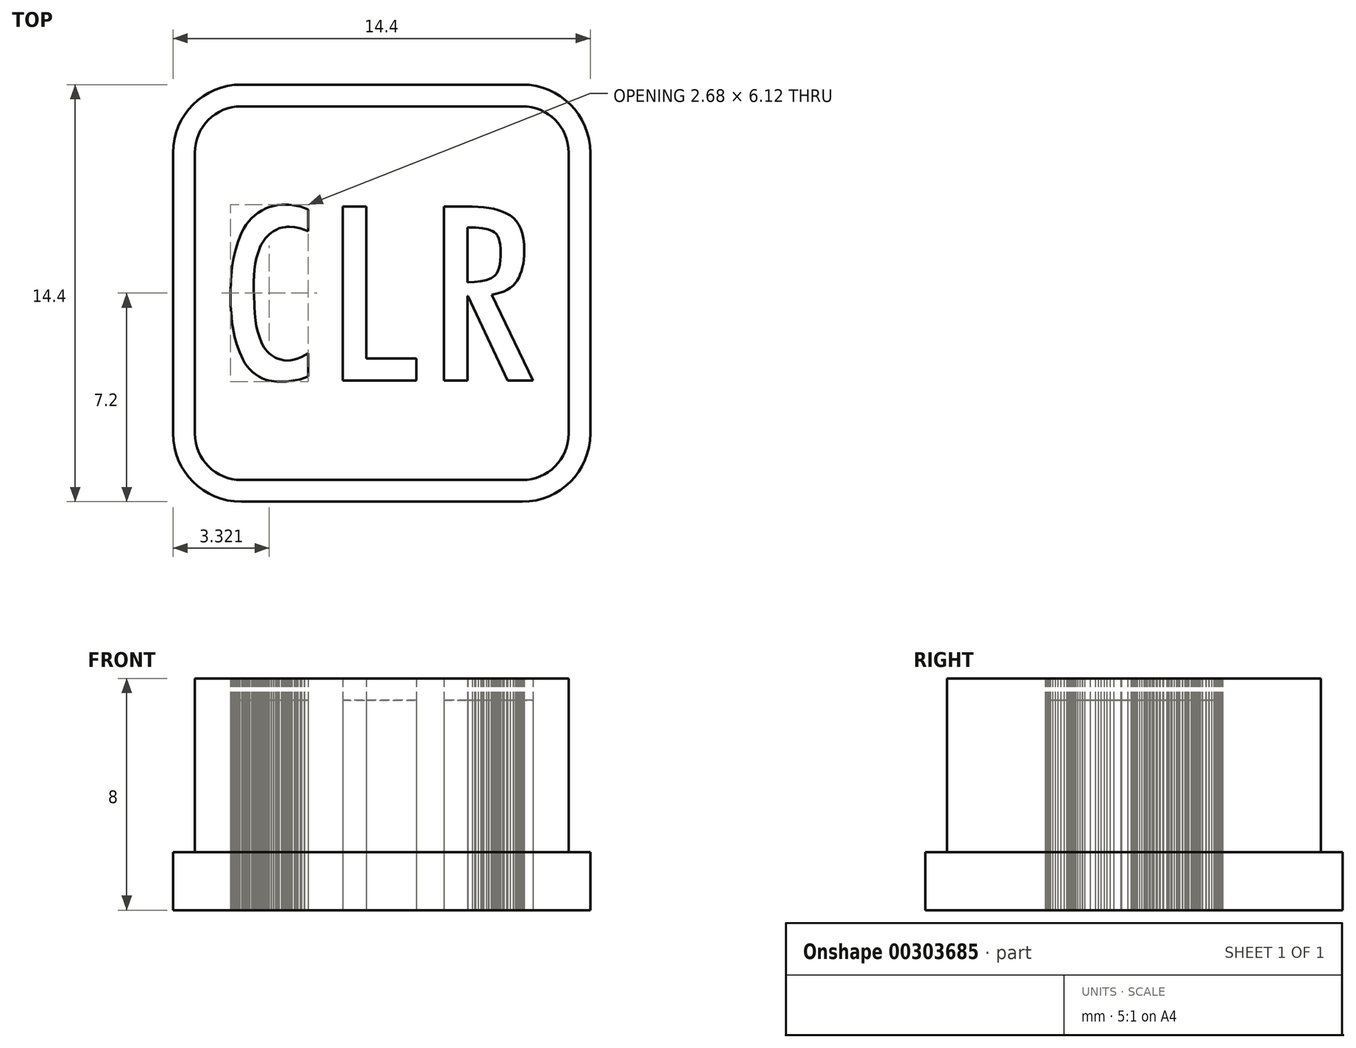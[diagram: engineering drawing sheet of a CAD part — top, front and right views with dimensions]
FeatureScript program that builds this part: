
annotation { "Feature Type Name" : "Feature", "Feature Type Description" : "" }
export const myFeature = defineFeature(function(context is Context, id is Id, definition is map)
    precondition{}
    {
        {
            var Q0;
            Q0=qCreatedBy(makeId("Top.planeOp"),FACE);
            var sketch = newSketch(context, id + "F0", { "sketchPlane" : qUnion([Q0])});
            skArc(sketch, "E0", {"start": v(4.85, -6.45) * mm, "mid": v(5.98, -5.98) * mm, "end": v(6.45, -4.85) * mm});
            skLineSegment(sketch, "E1", {"start": v(6.45, -4.85) * mm, "end": v(6.45, 4.85) * mm});
            skArc(sketch, "E2", {"start": v(6.45, 4.85) * mm, "mid": v(5.98, 5.98) * mm, "end": v(4.85, 6.45) * mm});
            skLineSegment(sketch, "E3", {"start": v(4.85, 6.45) * mm, "end": v(-4.85, 6.45) * mm});
            skArc(sketch, "E4", {"start": v(-4.85, 6.45) * mm, "mid": v(-5.98, 5.98) * mm, "end": v(-6.45, 4.85) * mm});
            skLineSegment(sketch, "E5", {"start": v(-6.45, 4.85) * mm, "end": v(-6.45, -4.85) * mm});
            skArc(sketch, "E6", {"start": v(-6.45, -4.85) * mm, "mid": v(-5.98, -5.98) * mm, "end": v(-4.85, -6.45) * mm});
            skLineSegment(sketch, "E7", {"start": v(-4.85, -6.45) * mm, "end": v(4.85, -6.45) * mm});
            skArc(sketch, "E8", {"start": v(-4.85, 7.2) * mm, "mid": v(-6.51, 6.51) * mm, "end": v(-7.2, 4.85) * mm});
            skLineSegment(sketch, "E9", {"start": v(-7.2, 4.85) * mm, "end": v(-7.2, -4.85) * mm});
            skArc(sketch, "E10", {"start": v(-7.2, -4.85) * mm, "mid": v(-6.51, -6.51) * mm, "end": v(-4.85, -7.2) * mm});
            skLineSegment(sketch, "E11", {"start": v(-4.85, -7.2) * mm, "end": v(4.85, -7.2) * mm});
            skArc(sketch, "E12", {"start": v(4.85, -7.2) * mm, "mid": v(6.51, -6.51) * mm, "end": v(7.2, -4.85) * mm});
            skLineSegment(sketch, "E13", {"start": v(7.2, -4.85) * mm, "end": v(7.2, 4.85) * mm});
            skArc(sketch, "E14", {"start": v(7.2, 4.85) * mm, "mid": v(6.51, 6.51) * mm, "end": v(4.85, 7.2) * mm});
            skLineSegment(sketch, "E15", {"start": v(4.85, 7.2) * mm, "end": v(-4.85, 7.2) * mm});
            skLineSegment(sketch, "E16", {"start": v(-2.54, -2.88) * mm, "end": v(-2.67, -2.93) * mm});
            skLineSegment(sketch, "E17", {"start": v(-2.67, -2.93) * mm, "end": v(-2.82, -2.97) * mm});
            skLineSegment(sketch, "E18", {"start": v(-2.82, -2.97) * mm, "end": v(-2.98, -3) * mm});
            skLineSegment(sketch, "E19", {"start": v(-2.98, -3) * mm, "end": v(-3.13, -3.03) * mm});
            skLineSegment(sketch, "E20", {"start": v(-3.13, -3.03) * mm, "end": v(-3.3, -3.05) * mm});
            skLineSegment(sketch, "E21", {"start": v(-3.3, -3.05) * mm, "end": v(-3.44, -3.06) * mm});
            skLineSegment(sketch, "E22", {"start": v(-3.44, -3.06) * mm, "end": v(-3.62, -3.05) * mm});
            skLineSegment(sketch, "E23", {"start": v(-3.62, -3.05) * mm, "end": v(-3.81, -3.03) * mm});
            skLineSegment(sketch, "E24", {"start": v(-3.81, -3.03) * mm, "end": v(-3.9, -3.02) * mm});
            skLineSegment(sketch, "E25", {"start": v(-3.9, -3.02) * mm, "end": v(-4, -3) * mm});
            skLineSegment(sketch, "E26", {"start": v(-4, -3) * mm, "end": v(-4.12, -2.94) * mm});
            skLineSegment(sketch, "E27", {"start": v(-4.12, -2.94) * mm, "end": v(-4.25, -2.88) * mm});
            skLineSegment(sketch, "E28", {"start": v(-4.25, -2.88) * mm, "end": v(-4.36, -2.8) * mm});
            skLineSegment(sketch, "E29", {"start": v(-4.36, -2.8) * mm, "end": v(-4.46, -2.72) * mm});
            skLineSegment(sketch, "E30", {"start": v(-4.46, -2.72) * mm, "end": v(-4.56, -2.63) * mm});
            skLineSegment(sketch, "E31", {"start": v(-4.56, -2.63) * mm, "end": v(-4.64, -2.53) * mm});
            skLineSegment(sketch, "E32", {"start": v(-4.64, -2.53) * mm, "end": v(-4.72, -2.41) * mm});
            skLineSegment(sketch, "E33", {"start": v(-4.72, -2.41) * mm, "end": v(-4.79, -2.3) * mm});
            skLineSegment(sketch, "E34", {"start": v(-4.79, -2.3) * mm, "end": v(-4.9, -2.04) * mm});
            skLineSegment(sketch, "E35", {"start": v(-4.9, -2.04) * mm, "end": v(-5, -1.78) * mm});
            skLineSegment(sketch, "E36", {"start": v(-5, -1.78) * mm, "end": v(-5.07, -1.5) * mm});
            skLineSegment(sketch, "E37", {"start": v(-5.07, -1.5) * mm, "end": v(-5.13, -1.23) * mm});
            skLineSegment(sketch, "E38", {"start": v(-5.13, -1.23) * mm, "end": v(-5.16, -1.03) * mm});
            skLineSegment(sketch, "E39", {"start": v(-5.16, -1.03) * mm, "end": v(-5.18, -0.82) * mm});
            skLineSegment(sketch, "E40", {"start": v(-5.18, -0.82) * mm, "end": v(-5.21, -0.43) * mm});
            skLineSegment(sketch, "E41", {"start": v(-5.21, -0.43) * mm, "end": v(-5.21, -0.32) * mm});
            skLineSegment(sketch, "E42", {"start": v(-5.21, -0.32) * mm, "end": v(-5.21, -0.21) * mm});
            skLineSegment(sketch, "E43", {"start": v(-5.21, -0.21) * mm, "end": v(-5.22, -0.1) * mm});
            skLineSegment(sketch, "E44", {"start": v(-5.22, -0.1) * mm, "end": v(-5.22, 0.02) * mm});
            skLineSegment(sketch, "E45", {"start": v(-5.22, 0.02) * mm, "end": v(-5.2, 0.45) * mm});
            skLineSegment(sketch, "E46", {"start": v(-5.2, 0.45) * mm, "end": v(-5.17, 0.9) * mm});
            skLineSegment(sketch, "E47", {"start": v(-5.17, 0.9) * mm, "end": v(-5.12, 1.2) * mm});
            skLineSegment(sketch, "E48", {"start": v(-5.12, 1.2) * mm, "end": v(-5.05, 1.5) * mm});
            skLineSegment(sketch, "E49", {"start": v(-5.05, 1.5) * mm, "end": v(-4.95, 1.8) * mm});
            skLineSegment(sketch, "E50", {"start": v(-4.95, 1.8) * mm, "end": v(-4.83, 2.09) * mm});
            skLineSegment(sketch, "E51", {"start": v(-4.83, 2.09) * mm, "end": v(-4.76, 2.23) * mm});
            skLineSegment(sketch, "E52", {"start": v(-4.76, 2.23) * mm, "end": v(-4.68, 2.35) * mm});
            skLineSegment(sketch, "E53", {"start": v(-4.68, 2.35) * mm, "end": v(-4.6, 2.47) * mm});
            skLineSegment(sketch, "E54", {"start": v(-4.6, 2.47) * mm, "end": v(-4.5, 2.58) * mm});
            skLineSegment(sketch, "E55", {"start": v(-4.5, 2.58) * mm, "end": v(-4.39, 2.68) * mm});
            skLineSegment(sketch, "E56", {"start": v(-4.39, 2.68) * mm, "end": v(-4.27, 2.77) * mm});
            skLineSegment(sketch, "E57", {"start": v(-4.27, 2.77) * mm, "end": v(-4.14, 2.85) * mm});
            skLineSegment(sketch, "E58", {"start": v(-4.14, 2.85) * mm, "end": v(-4, 2.92) * mm});
            skLineSegment(sketch, "E59", {"start": v(-4, 2.92) * mm, "end": v(-3.9, 2.96) * mm});
            skLineSegment(sketch, "E60", {"start": v(-3.9, 2.96) * mm, "end": v(-3.81, 3) * mm});
            skLineSegment(sketch, "E61", {"start": v(-3.81, 3) * mm, "end": v(-3.6, 3.04) * mm});
            skLineSegment(sketch, "E62", {"start": v(-3.6, 3.04) * mm, "end": v(-3.46, 3.05) * mm});
            skLineSegment(sketch, "E63", {"start": v(-3.46, 3.05) * mm, "end": v(-3.33, 3.06) * mm});
            skLineSegment(sketch, "E64", {"start": v(-3.33, 3.06) * mm, "end": v(-3.21, 3.05) * mm});
            skLineSegment(sketch, "E65", {"start": v(-3.21, 3.05) * mm, "end": v(-3.1, 3.04) * mm});
            skLineSegment(sketch, "E66", {"start": v(-3.1, 3.04) * mm, "end": v(-2.95, 3.02) * mm});
            skLineSegment(sketch, "E67", {"start": v(-2.95, 3.02) * mm, "end": v(-2.8, 2.99) * mm});
            skLineSegment(sketch, "E68", {"start": v(-2.8, 2.99) * mm, "end": v(-2.67, 2.95) * mm});
            skLineSegment(sketch, "E69", {"start": v(-2.67, 2.95) * mm, "end": v(-2.54, 2.9) * mm});
            skLineSegment(sketch, "E70", {"start": v(-2.54, 2.9) * mm, "end": v(-2.54, 2.13) * mm});
            skLineSegment(sketch, "E71", {"start": v(-2.54, 2.13) * mm, "end": v(-2.67, 2.19) * mm});
            skLineSegment(sketch, "E72", {"start": v(-2.67, 2.19) * mm, "end": v(-2.82, 2.24) * mm});
            skLineSegment(sketch, "E73", {"start": v(-2.82, 2.24) * mm, "end": v(-3, 2.28) * mm});
            skLineSegment(sketch, "E74", {"start": v(-3, 2.28) * mm, "end": v(-3.19, 2.3) * mm});
            skLineSegment(sketch, "E75", {"start": v(-3.19, 2.3) * mm, "end": v(-3.26, 2.3) * mm});
            skLineSegment(sketch, "E76", {"start": v(-3.26, 2.3) * mm, "end": v(-3.33, 2.28) * mm});
            skLineSegment(sketch, "E77", {"start": v(-3.33, 2.28) * mm, "end": v(-3.43, 2.26) * mm});
            skLineSegment(sketch, "E78", {"start": v(-3.43, 2.26) * mm, "end": v(-3.54, 2.24) * mm});
            skLineSegment(sketch, "E79", {"start": v(-3.54, 2.24) * mm, "end": v(-3.63, 2.2) * mm});
            skLineSegment(sketch, "E80", {"start": v(-3.63, 2.2) * mm, "end": v(-3.73, 2.13) * mm});
            skLineSegment(sketch, "E81", {"start": v(-3.73, 2.13) * mm, "end": v(-3.8, 2.08) * mm});
            skLineSegment(sketch, "E82", {"start": v(-3.8, 2.08) * mm, "end": v(-3.88, 2.03) * mm});
            skLineSegment(sketch, "E83", {"start": v(-3.88, 2.03) * mm, "end": v(-3.95, 1.97) * mm});
            skLineSegment(sketch, "E84", {"start": v(-3.95, 1.97) * mm, "end": v(-4.01, 1.9) * mm});
            skLineSegment(sketch, "E85", {"start": v(-4.01, 1.9) * mm, "end": v(-4.07, 1.83) * mm});
            skLineSegment(sketch, "E86", {"start": v(-4.07, 1.83) * mm, "end": v(-4.12, 1.75) * mm});
            skLineSegment(sketch, "E87", {"start": v(-4.12, 1.75) * mm, "end": v(-4.17, 1.66) * mm});
            skLineSegment(sketch, "E88", {"start": v(-4.17, 1.66) * mm, "end": v(-4.2, 1.58) * mm});
            skLineSegment(sketch, "E89", {"start": v(-4.2, 1.58) * mm, "end": v(-4.27, 1.4) * mm});
            skLineSegment(sketch, "E90", {"start": v(-4.27, 1.4) * mm, "end": v(-4.33, 1.2) * mm});
            skLineSegment(sketch, "E91", {"start": v(-4.33, 1.2) * mm, "end": v(-4.37, 1) * mm});
            skLineSegment(sketch, "E92", {"start": v(-4.37, 1) * mm, "end": v(-4.4, 0.8) * mm});
            skLineSegment(sketch, "E93", {"start": v(-4.4, 0.8) * mm, "end": v(-4.42, 0.42) * mm});
            skLineSegment(sketch, "E94", {"start": v(-4.42, 0.42) * mm, "end": v(-4.42, 0.05) * mm});
            skLineSegment(sketch, "E95", {"start": v(-4.42, 0.05) * mm, "end": v(-4.42, 0.03) * mm});
            skLineSegment(sketch, "E96", {"start": v(-4.42, 0.03) * mm, "end": v(-4.42, 0.03) * mm});
            skLineSegment(sketch, "E97", {"start": v(-4.42, 0.03) * mm, "end": v(-4.42, 0.01) * mm});
            skLineSegment(sketch, "E98", {"start": v(-4.42, 0.01) * mm, "end": v(-4.42, 0) * mm});
            skLineSegment(sketch, "E99", {"start": v(-4.42, 0) * mm, "end": v(-4.41, -0.02) * mm});
            skLineSegment(sketch, "E100", {"start": v(-4.41, -0.02) * mm, "end": v(-4.4, -0.03) * mm});
            skLineSegment(sketch, "E101", {"start": v(-4.4, -0.03) * mm, "end": v(-4.4, -0.46) * mm});
            skLineSegment(sketch, "E102", {"start": v(-4.4, -0.46) * mm, "end": v(-4.38, -0.7) * mm});
            skLineSegment(sketch, "E103", {"start": v(-4.38, -0.7) * mm, "end": v(-4.36, -0.94) * mm});
            skLineSegment(sketch, "E104", {"start": v(-4.36, -0.94) * mm, "end": v(-4.33, -1.14) * mm});
            skLineSegment(sketch, "E105", {"start": v(-4.33, -1.14) * mm, "end": v(-4.28, -1.33) * mm});
            skLineSegment(sketch, "E106", {"start": v(-4.28, -1.33) * mm, "end": v(-4.22, -1.52) * mm});
            skLineSegment(sketch, "E107", {"start": v(-4.22, -1.52) * mm, "end": v(-4.15, -1.7) * mm});
            skLineSegment(sketch, "E108", {"start": v(-4.15, -1.7) * mm, "end": v(-4.1, -1.79) * mm});
            skLineSegment(sketch, "E109", {"start": v(-4.1, -1.79) * mm, "end": v(-4.06, -1.87) * mm});
            skLineSegment(sketch, "E110", {"start": v(-4.06, -1.87) * mm, "end": v(-4, -1.94) * mm});
            skLineSegment(sketch, "E111", {"start": v(-4, -1.94) * mm, "end": v(-3.95, -2.01) * mm});
            skLineSegment(sketch, "E112", {"start": v(-3.95, -2.01) * mm, "end": v(-3.89, -2.07) * mm});
            skLineSegment(sketch, "E113", {"start": v(-3.89, -2.07) * mm, "end": v(-3.82, -2.13) * mm});
            skLineSegment(sketch, "E114", {"start": v(-3.82, -2.13) * mm, "end": v(-3.74, -2.18) * mm});
            skLineSegment(sketch, "E115", {"start": v(-3.74, -2.18) * mm, "end": v(-3.66, -2.23) * mm});
            skLineSegment(sketch, "E116", {"start": v(-3.66, -2.23) * mm, "end": v(-3.57, -2.27) * mm});
            skLineSegment(sketch, "E117", {"start": v(-3.57, -2.27) * mm, "end": v(-3.47, -2.3) * mm});
            skLineSegment(sketch, "E118", {"start": v(-3.47, -2.3) * mm, "end": v(-3.38, -2.32) * mm});
            skLineSegment(sketch, "E119", {"start": v(-3.38, -2.32) * mm, "end": v(-3.28, -2.33) * mm});
            skLineSegment(sketch, "E120", {"start": v(-3.28, -2.33) * mm, "end": v(-3.15, -2.32) * mm});
            skLineSegment(sketch, "E121", {"start": v(-3.15, -2.32) * mm, "end": v(-3.02, -2.3) * mm});
            skLineSegment(sketch, "E122", {"start": v(-3.02, -2.3) * mm, "end": v(-2.9, -2.25) * mm});
            skLineSegment(sketch, "E123", {"start": v(-2.9, -2.25) * mm, "end": v(-2.77, -2.2) * mm});
            skLineSegment(sketch, "E124", {"start": v(-2.77, -2.2) * mm, "end": v(-2.54, -2.08) * mm});
            skLineSegment(sketch, "E125", {"start": v(-2.54, -2.08) * mm, "end": v(-2.54, -2.88) * mm});
            skLineSegment(sketch, "E126", {"start": v(-1.35, -3.01) * mm, "end": v(-1.35, 2.99) * mm});
            skLineSegment(sketch, "E127", {"start": v(-1.35, 2.99) * mm, "end": v(-0.53, 2.99) * mm});
            skLineSegment(sketch, "E128", {"start": v(-0.53, 2.99) * mm, "end": v(-0.53, -2.25) * mm});
            skLineSegment(sketch, "E129", {"start": v(-0.53, -2.25) * mm, "end": v(1.2, -2.25) * mm});
            skLineSegment(sketch, "E130", {"start": v(1.2, -2.25) * mm, "end": v(1.2, -3.01) * mm});
            skLineSegment(sketch, "E131", {"start": v(1.2, -3.01) * mm, "end": v(-1.35, -3.01) * mm});
            skLineSegment(sketch, "E132", {"start": v(2.96, -0.1) * mm, "end": v(2.96, -3.01) * mm});
            skLineSegment(sketch, "E133", {"start": v(2.96, -3.01) * mm, "end": v(2.14, -3.01) * mm});
            skLineSegment(sketch, "E134", {"start": v(2.14, -3.01) * mm, "end": v(2.14, 2.99) * mm});
            skLineSegment(sketch, "E135", {"start": v(2.14, 2.99) * mm, "end": v(3.12, 2.99) * mm});
            skLineSegment(sketch, "E136", {"start": v(3.12, 2.99) * mm, "end": v(3.32, 2.98) * mm});
            skLineSegment(sketch, "E137", {"start": v(3.32, 2.98) * mm, "end": v(3.51, 2.97) * mm});
            skLineSegment(sketch, "E138", {"start": v(3.51, 2.97) * mm, "end": v(3.7, 2.94) * mm});
            skLineSegment(sketch, "E139", {"start": v(3.7, 2.94) * mm, "end": v(3.86, 2.9) * mm});
            skLineSegment(sketch, "E140", {"start": v(3.86, 2.9) * mm, "end": v(4.02, 2.87) * mm});
            skLineSegment(sketch, "E141", {"start": v(4.02, 2.87) * mm, "end": v(4.17, 2.81) * mm});
            skLineSegment(sketch, "E142", {"start": v(4.17, 2.81) * mm, "end": v(4.3, 2.75) * mm});
            skLineSegment(sketch, "E143", {"start": v(4.3, 2.75) * mm, "end": v(4.43, 2.68) * mm});
            skLineSegment(sketch, "E144", {"start": v(4.43, 2.68) * mm, "end": v(4.55, 2.6) * mm});
            skLineSegment(sketch, "E145", {"start": v(4.55, 2.6) * mm, "end": v(4.65, 2.49) * mm});
            skLineSegment(sketch, "E146", {"start": v(4.65, 2.49) * mm, "end": v(4.73, 2.36) * mm});
            skLineSegment(sketch, "E147", {"start": v(4.73, 2.36) * mm, "end": v(4.8, 2.22) * mm});
            skLineSegment(sketch, "E148", {"start": v(4.8, 2.22) * mm, "end": v(4.85, 2.06) * mm});
            skLineSegment(sketch, "E149", {"start": v(4.85, 2.06) * mm, "end": v(4.89, 1.88) * mm});
            skLineSegment(sketch, "E150", {"start": v(4.89, 1.88) * mm, "end": v(4.91, 1.68) * mm});
            skLineSegment(sketch, "E151", {"start": v(4.91, 1.68) * mm, "end": v(4.92, 1.46) * mm});
            skLineSegment(sketch, "E152", {"start": v(4.92, 1.46) * mm, "end": v(4.92, 1.3) * mm});
            skLineSegment(sketch, "E153", {"start": v(4.92, 1.3) * mm, "end": v(4.9, 1.16) * mm});
            skLineSegment(sketch, "E154", {"start": v(4.9, 1.16) * mm, "end": v(4.88, 1.02) * mm});
            skLineSegment(sketch, "E155", {"start": v(4.88, 1.02) * mm, "end": v(4.86, 0.9) * mm});
            skLineSegment(sketch, "E156", {"start": v(4.86, 0.9) * mm, "end": v(4.82, 0.77) * mm});
            skLineSegment(sketch, "E157", {"start": v(4.82, 0.77) * mm, "end": v(4.78, 0.65) * mm});
            skLineSegment(sketch, "E158", {"start": v(4.78, 0.65) * mm, "end": v(4.73, 0.54) * mm});
            skLineSegment(sketch, "E159", {"start": v(4.73, 0.54) * mm, "end": v(4.68, 0.44) * mm});
            skLineSegment(sketch, "E160", {"start": v(4.68, 0.44) * mm, "end": v(4.6, 0.35) * mm});
            skLineSegment(sketch, "E161", {"start": v(4.6, 0.35) * mm, "end": v(4.53, 0.26) * mm});
            skLineSegment(sketch, "E162", {"start": v(4.53, 0.26) * mm, "end": v(4.44, 0.19) * mm});
            skLineSegment(sketch, "E163", {"start": v(4.44, 0.19) * mm, "end": v(4.33, 0.12) * mm});
            skLineSegment(sketch, "E164", {"start": v(4.33, 0.12) * mm, "end": v(4.22, 0.06) * mm});
            skLineSegment(sketch, "E165", {"start": v(4.22, 0.06) * mm, "end": v(4.09, 0.01) * mm});
            skLineSegment(sketch, "E166", {"start": v(4.09, 0.01) * mm, "end": v(3.95, -0.03) * mm});
            skLineSegment(sketch, "E167", {"start": v(3.95, -0.03) * mm, "end": v(3.8, -0.05) * mm});
            skLineSegment(sketch, "E168", {"start": v(3.8, -0.05) * mm, "end": v(5.22, -3.01) * mm});
            skLineSegment(sketch, "E169", {"start": v(5.22, -3.01) * mm, "end": v(4.34, -3.01) * mm});
            skLineSegment(sketch, "E170", {"start": v(4.34, -3.01) * mm, "end": v(2.98, -0.1) * mm});
            skLineSegment(sketch, "E171", {"start": v(2.98, -0.1) * mm, "end": v(2.96, -0.1) * mm});
            skLineSegment(sketch, "E172", {"start": v(2.96, 2.27) * mm, "end": v(2.96, 0.38) * mm});
            skLineSegment(sketch, "E173", {"start": v(2.96, 0.38) * mm, "end": v(3.2, 0.38) * mm});
            skLineSegment(sketch, "E174", {"start": v(3.2, 0.38) * mm, "end": v(3.42, 0.41) * mm});
            skLineSegment(sketch, "E175", {"start": v(3.42, 0.41) * mm, "end": v(3.6, 0.46) * mm});
            skLineSegment(sketch, "E176", {"start": v(3.6, 0.46) * mm, "end": v(3.78, 0.52) * mm});
            skLineSegment(sketch, "E177", {"start": v(3.78, 0.52) * mm, "end": v(3.85, 0.56) * mm});
            skLineSegment(sketch, "E178", {"start": v(3.85, 0.56) * mm, "end": v(3.92, 0.62) * mm});
            skLineSegment(sketch, "E179", {"start": v(3.92, 0.62) * mm, "end": v(3.97, 0.7) * mm});
            skLineSegment(sketch, "E180", {"start": v(3.97, 0.7) * mm, "end": v(4.02, 0.78) * mm});
            skLineSegment(sketch, "E181", {"start": v(4.02, 0.78) * mm, "end": v(4.05, 0.88) * mm});
            skLineSegment(sketch, "E182", {"start": v(4.05, 0.88) * mm, "end": v(4.08, 1) * mm});
            skLineSegment(sketch, "E183", {"start": v(4.08, 1) * mm, "end": v(4.1, 1.13) * mm});
            skLineSegment(sketch, "E184", {"start": v(4.1, 1.13) * mm, "end": v(4.1, 1.27) * mm});
            skLineSegment(sketch, "E185", {"start": v(4.1, 1.27) * mm, "end": v(4.1, 1.38) * mm});
            skLineSegment(sketch, "E186", {"start": v(4.1, 1.38) * mm, "end": v(4.1, 1.53) * mm});
            skLineSegment(sketch, "E187", {"start": v(4.1, 1.53) * mm, "end": v(4.09, 1.67) * mm});
            skLineSegment(sketch, "E188", {"start": v(4.09, 1.67) * mm, "end": v(4.07, 1.79) * mm});
            skLineSegment(sketch, "E189", {"start": v(4.07, 1.79) * mm, "end": v(4.04, 1.89) * mm});
            skLineSegment(sketch, "E190", {"start": v(4.04, 1.89) * mm, "end": v(4, 1.98) * mm});
            skLineSegment(sketch, "E191", {"start": v(4, 1.98) * mm, "end": v(3.95, 2.05) * mm});
            skLineSegment(sketch, "E192", {"start": v(3.95, 2.05) * mm, "end": v(3.9, 2.1) * mm});
            skLineSegment(sketch, "E193", {"start": v(3.9, 2.1) * mm, "end": v(3.83, 2.14) * mm});
            skLineSegment(sketch, "E194", {"start": v(3.83, 2.14) * mm, "end": v(3.67, 2.2) * mm});
            skLineSegment(sketch, "E195", {"start": v(3.67, 2.2) * mm, "end": v(3.47, 2.24) * mm});
            skLineSegment(sketch, "E196", {"start": v(3.47, 2.24) * mm, "end": v(3.24, 2.26) * mm});
            skLineSegment(sketch, "E197", {"start": v(3.24, 2.26) * mm, "end": v(2.96, 2.27) * mm});
            skSolve(sketch);
        }
        {
            var Q0;
            Q0=makeQuery(id+"F0.imprint","IMPRINT",FACE,{"disambiguationData":[TD([[makeQuery(id+"F0.imprint","IMPRINT",EDGE,{"derivedFrom":sQuery(id+"F0.wireOp",EDGE,"E0")}),-1.0]])]});
            extrude(context, id + "F1", {"entities" : qUnion([Q0]), "depth" : 2 * mm});
        }
        {
            var Q0;
            Q0=makeQuery(id+"F0.imprint","IMPRINT",FACE,{"disambiguationData":[TD([[makeQuery(id+"F0.imprint","IMPRINT",EDGE,{"derivedFrom":sQuery(id+"F0.wireOp",EDGE,"E0")}),1.0]])]});
            var Q1;
            Q1=makeQuery(id+"F0.imprint","IMPRINT",FACE,{"disambiguationData":[TD([[makeQuery(id+"F0.imprint","IMPRINT",EDGE,{"derivedFrom":sQuery(id+"F0.wireOp",EDGE,"E172")}),1.0]])]});
            extrude(context, id + "F2", {"entities" : qUnion([Q0, Q1]), "operationType" : NewBodyOperationType.ADD, "depth" : 8 * mm});
        }
        {
            var Q0;
            Q0=makeQuery(id+"F0.imprint","IMPRINT",FACE,{"disambiguationData":[TD([[makeQuery(id+"F0.imprint","IMPRINT",EDGE,{"derivedFrom":sQuery(id+"F0.wireOp",EDGE,"E16")}),-1.0]])]});
            var Q1;
            Q1=makeQuery(id+"F0.imprint","IMPRINT",FACE,{"disambiguationData":[TD([[makeQuery(id+"F0.imprint","IMPRINT",EDGE,{"derivedFrom":sQuery(id+"F0.wireOp",EDGE,"E126")}),-1.0]])]});
            var Q2;
            Q2=makeQuery(id+"F0.imprint","IMPRINT",FACE,{"disambiguationData":[TD([[makeQuery(id+"F0.imprint","IMPRINT",EDGE,{"derivedFrom":sQuery(id+"F0.wireOp",EDGE,"E132")}),-1.0]])]});
            extrude(context, id + "F3", {"entities" : qUnion([Q0, Q1, Q2]), "depth" : 7.25 * mm});
        }
    });
